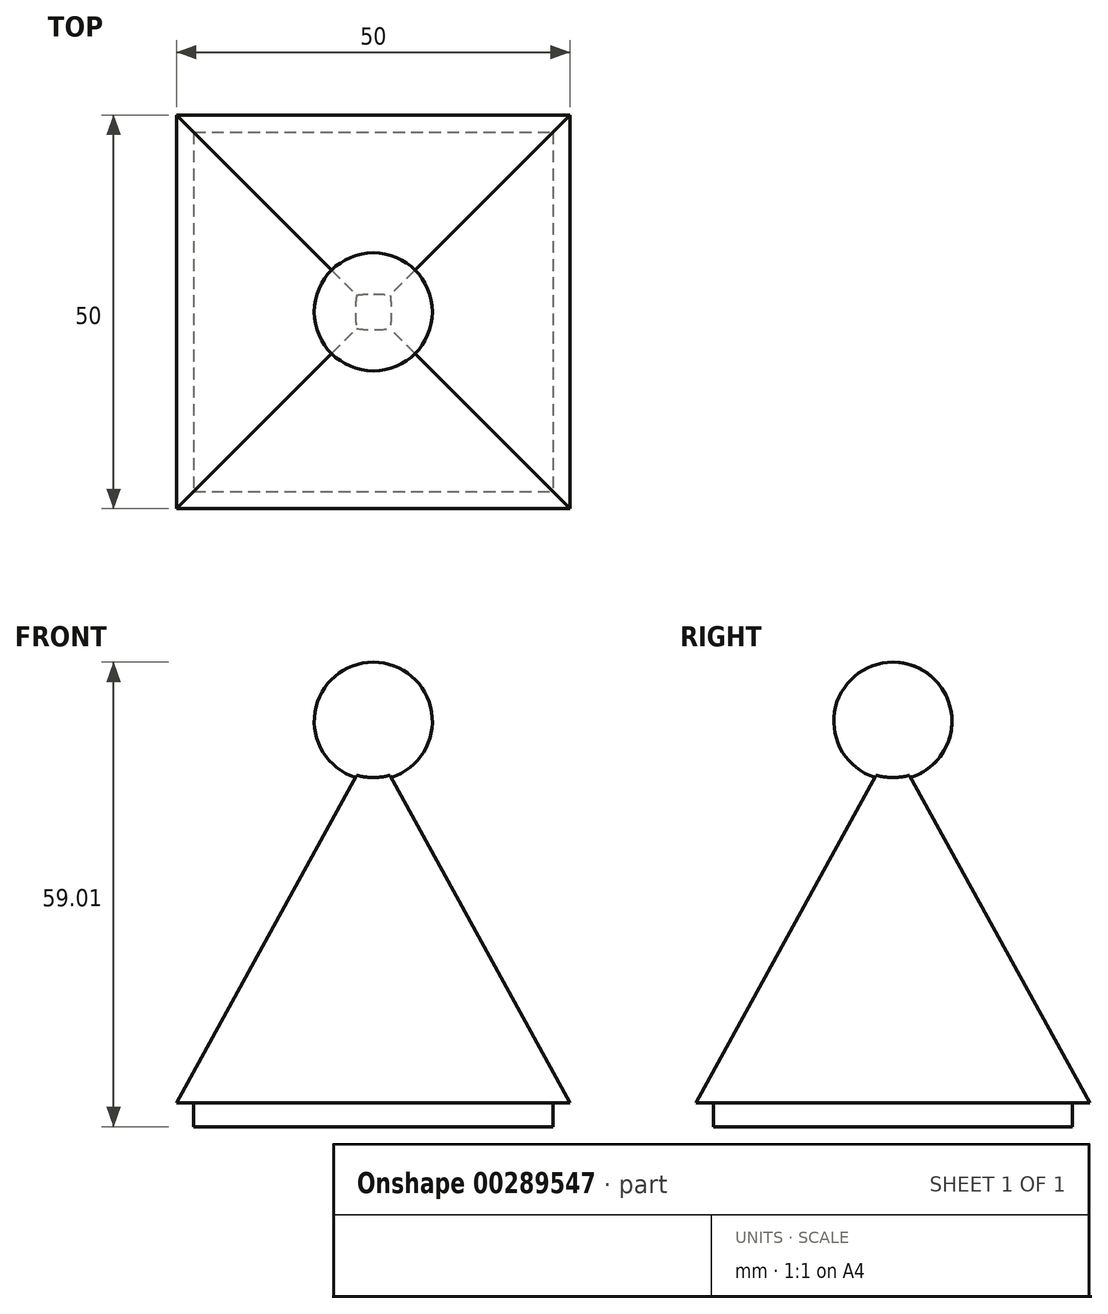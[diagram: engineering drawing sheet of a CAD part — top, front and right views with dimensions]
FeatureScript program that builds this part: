
annotation { "Feature Type Name" : "Feature", "Feature Type Description" : "" }
export const myFeature = defineFeature(function(context is Context, id is Id, definition is map)
    precondition{}
    {
        {
            var Q0;
            Q0=qCreatedBy(makeId("Top.planeOp"),FACE);
            var sketch = newSketch(context, id + "F0", { "sketchPlane" : qUnion([Q0])});
            skLineSegment(sketch, "E0.bottom", {"start": v(-25, 25) * mm, "end": v(25, 25) * mm});
            skLineSegment(sketch, "E0.top", {"start": v(-25, -25) * mm, "end": v(25, -25) * mm});
            skLineSegment(sketch, "E0.left", {"start": v(-25, 25) * mm, "end": v(-25, -25) * mm});
            skLineSegment(sketch, "E0.right", {"start": v(25, 25) * mm, "end": v(25, -25) * mm});
            skPoint(sketch, "E0.middle", {"position": v(0, 0) * mm});
            skSolve(sketch);
        }
        {
            var Q0;
            Q0=qCreatedBy(makeId("Front.planeOp"),FACE);
            var sketch = newSketch(context, id + "F1", { "sketchPlane" : qUnion([Q0])});
            skPoint(sketch, "E1", {"position": v(0, 45.52) * mm});
            skSolve(sketch);
        }
        {
            var Q0;
            Q0=makeQuery(id+"F0.imprint","IMPRINT",FACE,{"disambiguationData":[TD([[makeQuery(id+"F0.imprint","IMPRINT",EDGE,{"derivedFrom":sQuery(id+"F0.wireOp",EDGE,"E0.bottom")}),-1.0]])]});
            var Q1;
            Q1=sQuery(id+"F1.wireOp",VERTEX,"E1");
            loft(context, id + "F2", {"sheetProfilesArray" : [{ "sheetProfileEntities" : qUnion([Q0]) }, { "sheetProfileEntities" : qUnion([Q1]) }]});
        }
        {
            var Q0;
            Q0=qCreatedBy(makeId("Right.planeOp"),FACE);
            var sketch = newSketch(context, id + "F3", { "sketchPlane" : qUnion([Q0])});
            skArc(sketch, "E2", {"start": v(0, 56) * mm, "mid": v(-7.5, 48.5) * mm, "end": v(0, 41) * mm});
            skPoint(sketch, "E3.end.orphan", {"position": v(2.69, 48.5) * mm});
            skPoint(sketch, "E4.orphan", {"position": v(0, 56) * mm});
            skLineSegment(sketch, "E5", {"start": v(0, 56) * mm, "end": v(0, 41) * mm});
            skSolve(sketch);
        }
        {
            var Q0;
            Q0=makeQuery(id+"F3.imprint","IMPRINT",FACE,{"disambiguationData":[TD([[makeQuery(id+"F3.imprint","IMPRINT",EDGE,{"derivedFrom":sQuery(id+"F3.wireOp",EDGE,"E2")}),1.0]])]});
            var Q1;
            Q1=sQuery(id+"F3.wireOp",EDGE,"E5");
            revolve(context, id + "F4", {"operationType" : NewBodyOperationType.ADD, "entities" : qUnion([Q0]), "axis" : qUnion([Q1]), "revolveType" : RevolveType.FULL});
        }
        {
            var Q0;
            Q0=qCreatedBy(makeId("Top.planeOp"),FACE);
            var sketch = newSketch(context, id + "F5", { "sketchPlane" : qUnion([Q0])});
            skLineSegment(sketch, "E6.bottom", {"start": v(-22.8, 22.8) * mm, "end": v(22.8, 22.8) * mm});
            skLineSegment(sketch, "E6.top", {"start": v(-22.8, -22.8) * mm, "end": v(22.8, -22.8) * mm});
            skLineSegment(sketch, "E6.left", {"start": v(-22.8, 22.8) * mm, "end": v(-22.8, -22.8) * mm});
            skLineSegment(sketch, "E6.right", {"start": v(22.8, 22.8) * mm, "end": v(22.8, -22.8) * mm});
            skPoint(sketch, "E6.middle", {"position": v(0, 0) * mm});
            skSolve(sketch);
        }
        {
            var Q0;
            Q0=makeQuery(id+"F5.imprint","IMPRINT",FACE,{"disambiguationData":[TD([[makeQuery(id+"F5.imprint","IMPRINT",EDGE,{"derivedFrom":sQuery(id+"F5.wireOp",EDGE,"E6.bottom")}),-1.0]])]});
            extrude(context, id + "F6", {"entities" : qUnion([Q0]), "operationType" : NewBodyOperationType.ADD, "oppositeDirection" : true, "depth" : 3 * mm});
        }
    });
